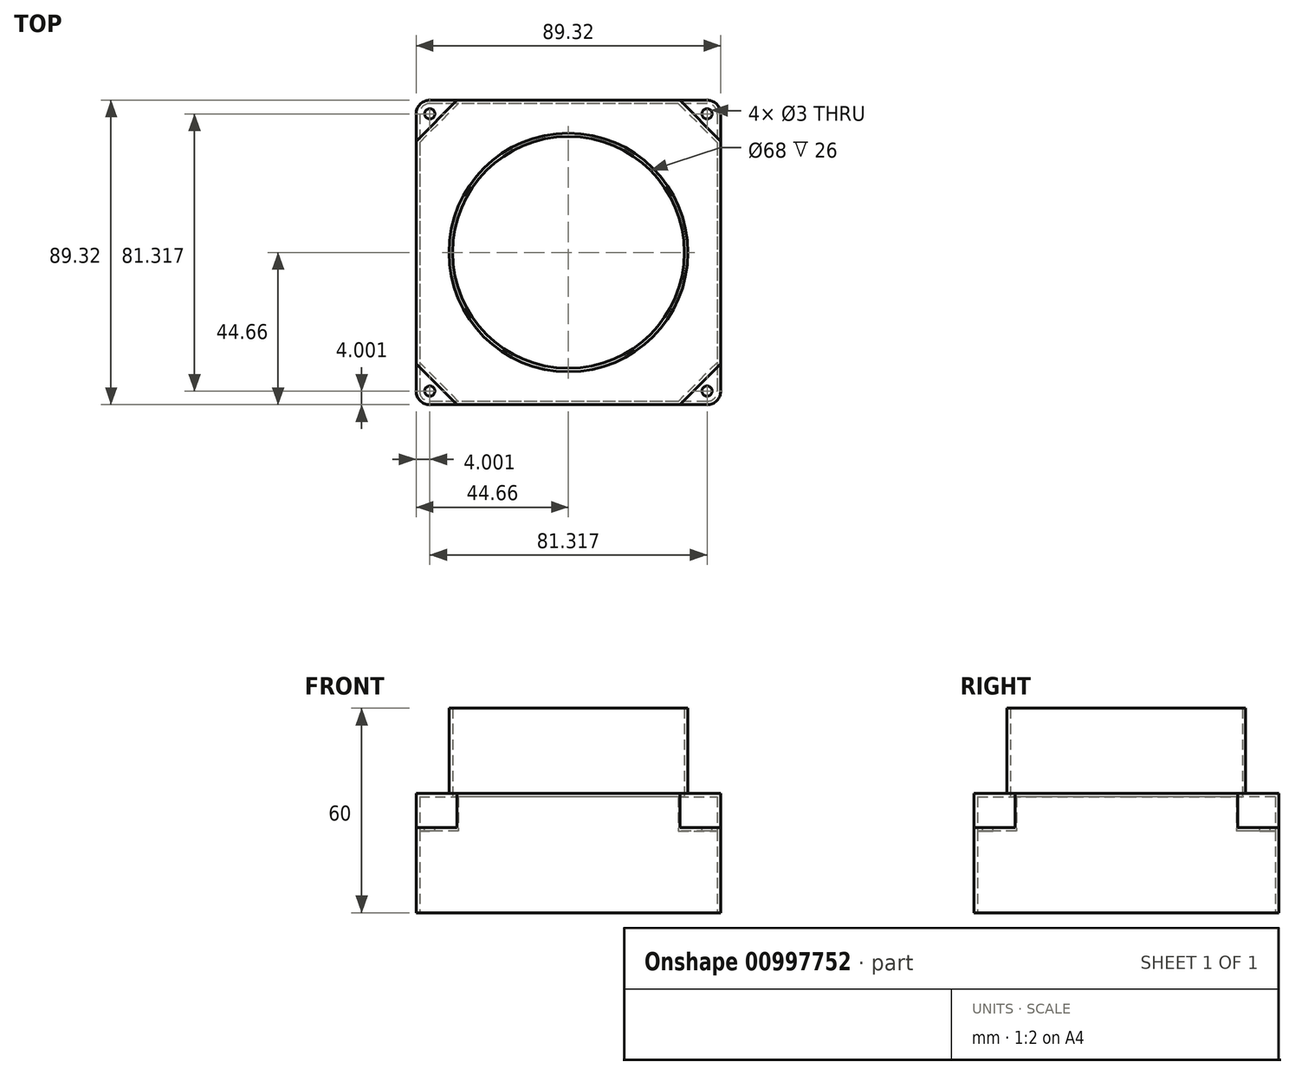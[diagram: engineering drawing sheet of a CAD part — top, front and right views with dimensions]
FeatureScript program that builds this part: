
annotation { "Feature Type Name" : "Feature", "Feature Type Description" : "" }
export const myFeature = defineFeature(function(context is Context, id is Id, definition is map)
    precondition{}
    {
        {
            var Q0;
            Q0=qCreatedBy(makeId("Top.planeOp"),FACE);
            var sketch = newSketch(context, id + "F0", { "sketchPlane" : qUnion([Q0])});
            skLineSegment(sketch, "E0.bottom", {"start": v(44.66, 44.66) * mm, "end": v(-44.66, 44.66) * mm});
            skLineSegment(sketch, "E0.top", {"start": v(44.66, -44.66) * mm, "end": v(-44.66, -44.66) * mm});
            skLineSegment(sketch, "E0.left", {"start": v(44.66, 44.66) * mm, "end": v(44.66, -44.66) * mm});
            skLineSegment(sketch, "E0.right", {"start": v(-44.66, 44.66) * mm, "end": v(-44.66, -44.66) * mm});
            skPoint(sketch, "E0.middle", {"position": v(0, 0) * mm});
            skSolve(sketch);
        }
        {
            var Q0;
            Q0=makeQuery(id+"F0.imprint","IMPRINT",FACE,{"disambiguationData":[TD([[makeQuery(id+"F0.imprint","IMPRINT",EDGE,{"derivedFrom":sQuery(id+"F0.wireOp",EDGE,"E0.bottom")}),1.0]])]});
            extrude(context, id + "F1", {"entities" : qUnion([Q0]), "depth" : 25 * mm, "offsetDistance" : 25 * mm});
        }
        {
            var Q0;
            Q0=makeQuery(id+"F1.opExtrude","CAP_FACE",FACE,{"disambiguationData":[OSD([sQuery(id+"F0.wireOp",EDGE,"E0.bottom"),sQuery(id+"F0.wireOp",EDGE,"E0.top"),sQuery(id+"F0.wireOp",EDGE,"E0.left"),sQuery(id+"F0.wireOp",EDGE,"E0.right")])],"isStart":false});
            var sketch = newSketch(context, id + "F2", { "sketchPlane" : qUnion([Q0])});
            skCircle(sketch, "E1.cCircle", {"center": v(0, 0) * mm, "radius": 54.67 * mm, "construction": true});
            skLineSegment(sketch, "E1.0", {"start": v(-22.65, 54.67) * mm, "end": v(22.65, 54.67) * mm});
            skLineSegment(sketch, "E1.1", {"start": v(22.65, 54.67) * mm, "end": v(54.67, 22.65) * mm});
            skLineSegment(sketch, "E1.2", {"start": v(54.67, 22.65) * mm, "end": v(54.67, -22.65) * mm});
            skLineSegment(sketch, "E1.3", {"start": v(54.67, -22.65) * mm, "end": v(22.65, -54.67) * mm});
            skLineSegment(sketch, "E1.4", {"start": v(22.65, -54.67) * mm, "end": v(-22.65, -54.67) * mm});
            skLineSegment(sketch, "E1.5", {"start": v(-22.65, -54.67) * mm, "end": v(-54.67, -22.65) * mm});
            skLineSegment(sketch, "E1.6", {"start": v(-54.67, -22.65) * mm, "end": v(-54.67, 22.65) * mm});
            skLineSegment(sketch, "E1.7", {"start": v(-54.67, 22.65) * mm, "end": v(-22.65, 54.67) * mm});
            skPoint(sketch, "E1.0.midPoint", {"position": v(0, 54.67) * mm});
            skPoint(sketch, "E2", {"position": v(44.66, 32.66) * mm});
            skSolve(sketch);
        }
        {
            var Q0;
            {var subQ3=makeQuery(id+"F1.opExtrude","CAP_EDGE",EDGE,{"disambiguationData":[OSD([sQuery(id+"F0.wireOp",EDGE,"E0.bottom")])],"isStart":false});var subQ13=sQuery(id+"F2.wireOp",EDGE,"E1.1");var subQ14=makeQuery(id+"F2.imprint","INTERSECT",VERTEX,{"derivedFrom":[subQ3,subQ13]});Q0=makeQuery(id+"F2.imprint","IMPRINT",FACE,{"disambiguationData":[TD([[makeQuery(id+"F2.imprint","IMPRINT",EDGE,{"disambiguationData":[TD([[subQ14,-1.0]])],"derivedFrom":subQ13}),-1.0]])]});}
            extrude(context, id + "F3", {"entities" : qUnion([Q0]), "operationType" : NewBodyOperationType.ADD, "depth" : 10 * mm, "offsetDistance" : 25 * mm});
        }
        {
            var Q0;
            Q0=makeQuery(id+"F3.opExtrude","CAP_FACE",FACE,{"disambiguationData":[OSD([sQuery(id+"F0.wireOp",EDGE,"E0.bottom"),sQuery(id+"F0.wireOp",EDGE,"E0.top"),sQuery(id+"F0.wireOp",EDGE,"E0.left"),sQuery(id+"F0.wireOp",EDGE,"E0.right"),sQuery(id+"F2.wireOp",EDGE,"E1.1"),sQuery(id+"F2.wireOp",EDGE,"E1.3"),sQuery(id+"F2.wireOp",EDGE,"E1.5"),sQuery(id+"F2.wireOp",EDGE,"E1.7")])],"isStart":false});
            var sketch = newSketch(context, id + "F4", { "sketchPlane" : qUnion([Q0])});
            skCircle(sketch, "E3", {"center": v(0, 0) * mm, "radius": 35 * mm});
            skSolve(sketch);
        }
        {
            var Q0;
            Q0=makeQuery(id+"F4.imprint","IMPRINT",FACE,{"disambiguationData":[TD([[makeQuery(id+"F4.imprint","IMPRINT",EDGE,{"derivedFrom":sQuery(id+"F4.wireOp",EDGE,"E3")}),1.0]])]});
            extrude(context, id + "F5", {"entities" : qUnion([Q0]), "operationType" : NewBodyOperationType.ADD, "depth" : 25 * mm, "offsetDistance" : 25 * mm});
        }
        {
            var Q0;
            Q0=makeQuery(id+"F1.opExtrude","SWEPT_EDGE",EDGE,{"disambiguationData":[OSD([sQuery(id+"F0.wireOp",EDGE,"E0.bottom"),sQuery(id+"F0.wireOp",EDGE,"E0.left")])]});
            var Q1;
            Q1=makeQuery(id+"F1.opExtrude","SWEPT_EDGE",EDGE,{"disambiguationData":[OSD([sQuery(id+"F0.wireOp",EDGE,"E0.top"),sQuery(id+"F0.wireOp",EDGE,"E0.left")])]});
            var Q2;
            Q2=makeQuery(id+"F1.opExtrude","SWEPT_EDGE",EDGE,{"disambiguationData":[OSD([sQuery(id+"F0.wireOp",EDGE,"E0.top"),sQuery(id+"F0.wireOp",EDGE,"E0.right")])]});
            var Q3;
            Q3=makeQuery(id+"F1.opExtrude","SWEPT_EDGE",EDGE,{"disambiguationData":[OSD([sQuery(id+"F0.wireOp",EDGE,"E0.bottom"),sQuery(id+"F0.wireOp",EDGE,"E0.right")])]});
            fillet(context, id + "F6", {"entities" : qUnion([Q0, Q1, Q2, Q3]), "radius" : 4 * mm, "tangentPropagation" : true, "allowEdgeOverflow" : false});
        }
        {
            var Q0;
            Q0=makeQuery(id+"F1.opExtrude","CAP_FACE",FACE,{"disambiguationData":[OSD([sQuery(id+"F0.wireOp",EDGE,"E0.bottom"),sQuery(id+"F0.wireOp",EDGE,"E0.top"),sQuery(id+"F0.wireOp",EDGE,"E0.left"),sQuery(id+"F0.wireOp",EDGE,"E0.right")])],"isStart":true});
            shell(context, id + "F7", {"entities" : qUnion([Q0]), "thickness" : 1 * mm});
        }
        {
            var Q0;
            {var subQ0=sQuery(id+"F4.wireOp",EDGE,"E3");Q0=makeQuery(id+"F7.opShell","OFFSET_FACE",FACE,{"disambiguationData":[OSD([subQ0]),TDD([makeQuery(id+"F5.opExtrude","CAP_FACE",FACE,{"disambiguationData":[OSD([subQ0])],"isStart":false})])]});}
            extrude(context, id + "F8", {"entities" : qUnion([Q0]), "operationType" : NewBodyOperationType.REMOVE, "oppositeDirection" : true, "depth" : 41.7 * mm, "offsetDistance" : 25 * mm});
        }
        {
            var Q0;
            {var subQ0=sQuery(id+"F0.wireOp",EDGE,"E0.bottom");var subQ1=sQuery(id+"F0.wireOp",EDGE,"E0.right");Q0=makeQuery(id+"F3.boolean.opBoolean","SPLIT",FACE,{"disambiguationData":[TD([makeQuery(id+"F3.opExtrude","SWEPT_FACE",FACE,{"disambiguationData":[OSD([sQuery(id+"F2.wireOp",EDGE,"E1.7")])]})])],"derivedFrom":makeQuery(id+"F1.opExtrude","CAP_FACE",FACE,{"disambiguationData":[OSD([subQ0,sQuery(id+"F0.wireOp",EDGE,"E0.top"),sQuery(id+"F0.wireOp",EDGE,"E0.left"),subQ1])],"isStart":false})});}
            var sketch = newSketch(context, id + "F9", { "sketchPlane" : qUnion([Q0])});
            skCircle(sketch, "E4", {"center": v(-40.66, 40.66) * mm, "radius": 1.5 * mm});
            skSolve(sketch);
        }
        {
            var Q0;
            Q0=makeQuery(id+"F9.imprint","IMPRINT",FACE,{"disambiguationData":[TD([[makeQuery(id+"F9.imprint","IMPRINT",EDGE,{"derivedFrom":sQuery(id+"F9.wireOp",EDGE,"E4")}),1.0]])]});
            extrude(context, id + "F10", {"entities" : qUnion([Q0]), "endBound" : BoundingType.SYMMETRIC, "oppositeDirection" : true, "depth" : 7.6 * mm, "offsetDistance" : 25 * mm});
        }
        {
            var Q0;
            Q0=qCreatedBy(makeId("Front.planeOp"),FACE);
            var sketch = newSketch(context, id + "F11", { "sketchPlane" : qUnion([Q0])});
            skPoint(sketch, "E5", {"position": v(0, 0) * mm});
            skLineSegment(sketch, "E6", {"start": v(0, 0) * mm, "end": v(0, 38.6) * mm});
            skSolve(sketch);
        }
        {
            var Q0;
            Q0=makeQuery(id+"F10.opExtrude","SWEPT_BODY",BODY,{"disambiguationData":[OSD([sQuery(id+"F9.wireOp",EDGE,"E4")])]});
            var Q1;
            Q1=sQuery(id+"F11.wireOp",EDGE,"E6");
            circularPattern(context, id + "F12", {"entities" : qUnion([Q0]), "axis" : qUnion([Q1]), "angle" : 360 * degree, "instanceCount" : 4, "equalSpace" : true});
        }
        {
            var Q0;
            Q0=makeQuery(id+"F10.opExtrude","SWEPT_BODY",BODY,{"disambiguationData":[OSD([sQuery(id+"F9.wireOp",EDGE,"E4")])]});
            var Q1;
            Q1=makeQuery(id+"F12.opPattern","COPY",BODY,{"derivedFrom":makeQuery(id+"F10.opExtrude","SWEPT_BODY",BODY,{"disambiguationData":[OSD([sQuery(id+"F9.wireOp",EDGE,"E4")])]}),"instanceName":"3"});
            var Q2;
            Q2=makeQuery(id+"F12.opPattern","COPY",BODY,{"derivedFrom":makeQuery(id+"F10.opExtrude","SWEPT_BODY",BODY,{"disambiguationData":[OSD([sQuery(id+"F9.wireOp",EDGE,"E4")])]}),"instanceName":"2"});
            var Q3;
            Q3=makeQuery(id+"F12.opPattern","COPY",BODY,{"derivedFrom":makeQuery(id+"F10.opExtrude","SWEPT_BODY",BODY,{"disambiguationData":[OSD([sQuery(id+"F9.wireOp",EDGE,"E4")])]}),"instanceName":"1"});
            var Q4;
            Q4=makeQuery(id+"F1.opExtrude","SWEPT_BODY",BODY,{"disambiguationData":[OSD([sQuery(id+"F0.wireOp",EDGE,"E0.bottom"),sQuery(id+"F0.wireOp",EDGE,"E0.top"),sQuery(id+"F0.wireOp",EDGE,"E0.left"),sQuery(id+"F0.wireOp",EDGE,"E0.right")])]});
            booleanBodies(context, id + "F13", {"operationType" : BooleanOperationType.SUBTRACTION, "tools" : qUnion([Q0, Q1, Q2, Q3]), "targets" : qUnion([Q4])});
        }
    });
